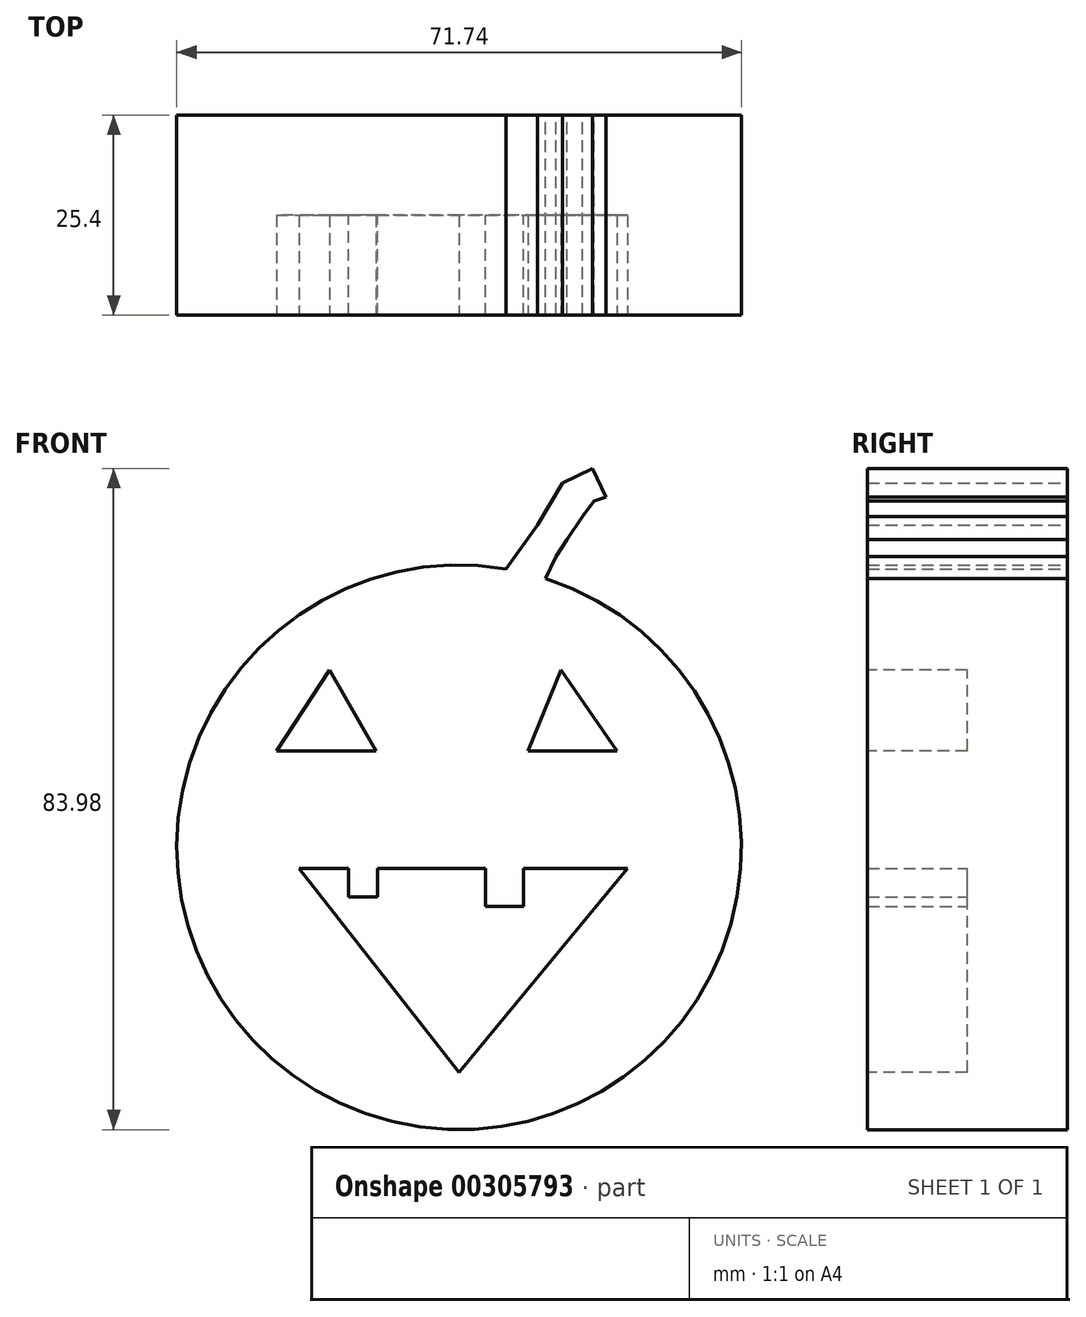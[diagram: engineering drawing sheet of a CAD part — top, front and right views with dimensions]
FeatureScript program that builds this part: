
annotation { "Feature Type Name" : "Feature", "Feature Type Description" : "" }
export const myFeature = defineFeature(function(context is Context, id is Id, definition is map)
    precondition{}
    {
        {
            var Q0;
            Q0=qCreatedBy(makeId("Front.planeOp"),FACE);
            var sketch = newSketch(context, id + "F0", { "sketchPlane" : qUnion([Q0])});
            skCircle(sketch, "E0", {"center": v(0, 0) * mm, "radius": 35.87 * mm});
            skLineSegment(sketch, "E1", {"start": v(11, 34.14) * mm, "end": v(12.28, 36.96) * mm});
            skLineSegment(sketch, "E2", {"start": v(12.28, 36.96) * mm, "end": v(13.72, 39.11) * mm});
            skLineSegment(sketch, "E3", {"start": v(13.72, 39.11) * mm, "end": v(15.7, 42) * mm});
            skLineSegment(sketch, "E4", {"start": v(15.7, 42) * mm, "end": v(17.14, 43.97) * mm});
            skLineSegment(sketch, "E5", {"start": v(17.14, 43.97) * mm, "end": v(18.65, 44.5) * mm});
            skLineSegment(sketch, "E6", {"start": v(18.65, 44.5) * mm, "end": v(16.95, 48.1) * mm});
            skLineSegment(sketch, "E7", {"start": v(16.95, 48.1) * mm, "end": v(13.13, 46.3) * mm});
            skPoint(sketch, "E7.endSnap0", {"position": v(17.8, 46.3) * mm});
            skLineSegment(sketch, "E8", {"start": v(13.13, 46.3) * mm, "end": v(9.94, 40.91) * mm});
            skLineSegment(sketch, "E9", {"start": v(9.94, 40.91) * mm, "end": v(5.96, 35.37) * mm});
            skSolve(sketch);
        }
        {
            var Q0;
            Q0 = qSketchRegion(id + "F0", true);
            extrude(context, id + "F1", {"entities" : qUnion([Q0]), "depth" : 25.4 * mm});
        }
        {
            var Q0;
            Q0=makeQuery(id+"F1.opExtrude","CAP_FACE",FACE,{"disambiguationData":[OSD([sQuery(id+"F0.wireOp",EDGE,"E0"),sQuery(id+"F0.wireOp",EDGE,"E1"),sQuery(id+"F0.wireOp",EDGE,"E2"),sQuery(id+"F0.wireOp",EDGE,"E3"),sQuery(id+"F0.wireOp",EDGE,"E4"),sQuery(id+"F0.wireOp",EDGE,"E5"),sQuery(id+"F0.wireOp",EDGE,"E6"),sQuery(id+"F0.wireOp",EDGE,"E7"),sQuery(id+"F0.wireOp",EDGE,"E8"),sQuery(id+"F0.wireOp",EDGE,"E9")])],"isStart":false});
            var sketch = newSketch(context, id + "F2", { "sketchPlane" : qUnion([Q0])});
            skLineSegment(sketch, "E10", {"start": v(-16.44, 22.5) * mm, "end": v(-23.22, 12.25) * mm});
            skLineSegment(sketch, "E11", {"start": v(-23.22, 12.25) * mm, "end": v(-10.56, 12.25) * mm});
            skLineSegment(sketch, "E12", {"start": v(-10.56, 12.25) * mm, "end": v(-16.44, 22.5) * mm});
            skLineSegment(sketch, "E13", {"start": v(12.95, 22.5) * mm, "end": v(8.73, 12.25) * mm});
            skLineSegment(sketch, "E14", {"start": v(8.73, 12.25) * mm, "end": v(20.03, 12.25) * mm});
            skLineSegment(sketch, "E15", {"start": v(20.03, 12.25) * mm, "end": v(12.95, 22.5) * mm});
            skLineSegment(sketch, "E16", {"start": v(-20.5, -4.03) * mm, "end": v(21.99, -4.03) * mm});
            skLineSegment(sketch, "E17", {"start": v(21.99, -4.03) * mm, "end": v(21.99, -8.85) * mm});
            skLineSegment(sketch, "E18", {"start": v(21.99, -8.85) * mm, "end": v(16.38, -12.72) * mm});
            skLineSegment(sketch, "E19", {"start": v(16.38, -12.72) * mm, "end": v(5.86, -14.27) * mm});
            skLineSegment(sketch, "E20", {"start": v(5.86, -14.27) * mm, "end": v(-6.04, -14.27) * mm});
            skLineSegment(sketch, "E21", {"start": v(-6.04, -14.27) * mm, "end": v(-15.84, -11.56) * mm});
            skLineSegment(sketch, "E22", {"start": v(-15.84, -11.56) * mm, "end": v(-20.55, -4.74) * mm});
            skSolve(sketch);
        }
        {
            var Q0;
            Q0 = qSketchRegion(id + "F2", true);
            extrude(context, id + "F3", {"entities" : qUnion([Q0]), "operationType" : NewBodyOperationType.REMOVE, "oppositeDirection" : true, "depth" : 12.7 * mm});
        }
        {
            var Q0;
            Q0=makeQuery(id+"F1.opExtrude","CAP_FACE",FACE,{"disambiguationData":[OSD([sQuery(id+"F0.wireOp",EDGE,"E0"),sQuery(id+"F0.wireOp",EDGE,"E1"),sQuery(id+"F0.wireOp",EDGE,"E2"),sQuery(id+"F0.wireOp",EDGE,"E3"),sQuery(id+"F0.wireOp",EDGE,"E4"),sQuery(id+"F0.wireOp",EDGE,"E5"),sQuery(id+"F0.wireOp",EDGE,"E6"),sQuery(id+"F0.wireOp",EDGE,"E7"),sQuery(id+"F0.wireOp",EDGE,"E8"),sQuery(id+"F0.wireOp",EDGE,"E9")])],"isStart":false});
            var sketch = newSketch(context, id + "F4", { "sketchPlane" : qUnion([Q0])});
            skLineSegment(sketch, "E23", {"start": v(-20.36, -2.67) * mm, "end": v(21.39, -2.67) * mm});
            skLineSegment(sketch, "E24", {"start": v(21.39, -2.67) * mm, "end": v(0, -28.6) * mm});
            skLineSegment(sketch, "E25", {"start": v(0, -28.6) * mm, "end": v(-20.36, -2.67) * mm});
            skSolve(sketch);
        }
        {
            var Q0;
            Q0 = qSketchRegion(id + "F4", true);
            extrude(context, id + "F5", {"entities" : qUnion([Q0]), "operationType" : NewBodyOperationType.REMOVE, "oppositeDirection" : true, "depth" : 12.7 * mm});
        }
        {
            var Q0;
            Q0=makeQuery(id+"F5.boolean.opBoolean","COPY",FACE,{"derivedFrom":makeQuery(id+"F5.opExtrude","CAP_FACE",FACE,{"disambiguationData":[OSD([sQuery(id+"F4.wireOp",EDGE,"E23"),sQuery(id+"F4.wireOp",EDGE,"E24"),sQuery(id+"F4.wireOp",EDGE,"E25")])],"isStart":false})});
            var sketch = newSketch(context, id + "F6", { "sketchPlane" : qUnion([Q0])});
            skLineSegment(sketch, "E26", {"start": v(-14.03, -2.67) * mm, "end": v(-14.03, -6.29) * mm});
            skLineSegment(sketch, "E27", {"start": v(-14.03, -6.29) * mm, "end": v(-10.38, -6.29) * mm});
            skLineSegment(sketch, "E28", {"start": v(-10.38, -6.29) * mm, "end": v(-10.38, -2.67) * mm});
            skLineSegment(sketch, "E29", {"start": v(-10.38, -2.67) * mm, "end": v(-14.03, -2.67) * mm});
            skLineSegment(sketch, "E30", {"start": v(3.35, -2.67) * mm, "end": v(3.35, -7.5) * mm});
            skLineSegment(sketch, "E31", {"start": v(3.35, -7.5) * mm, "end": v(8.16, -7.5) * mm});
            skLineSegment(sketch, "E32", {"start": v(8.16, -7.5) * mm, "end": v(8.16, -2.67) * mm});
            skLineSegment(sketch, "E33", {"start": v(8.16, -2.67) * mm, "end": v(3.35, -2.67) * mm});
            skSolve(sketch);
        }
        {
            var Q0;
            Q0 = qSketchRegion(id + "F6", true);
            extrude(context, id + "F7", {"entities" : qUnion([Q0]), "operationType" : NewBodyOperationType.ADD, "depth" : 12.7 * mm});
        }
    });
